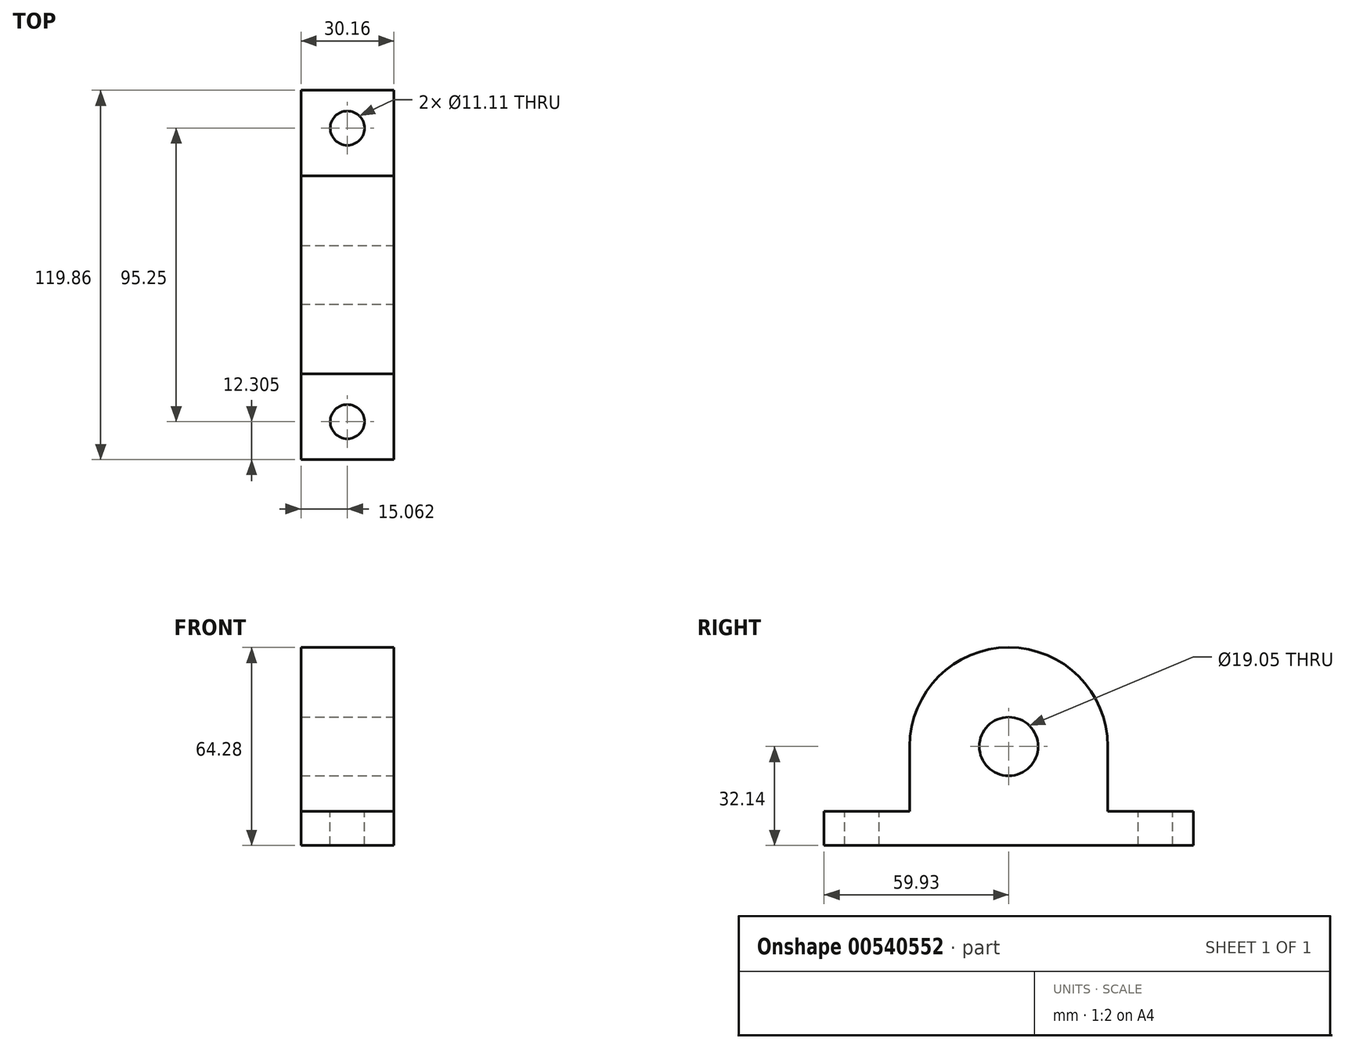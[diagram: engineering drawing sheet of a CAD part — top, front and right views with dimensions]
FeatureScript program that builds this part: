
annotation { "Feature Type Name" : "Feature", "Feature Type Description" : "" }
export const myFeature = defineFeature(function(context is Context, id is Id, definition is map)
    precondition{}
    {
        {
            var Q0;
            Q0=qCreatedBy(makeId("Right.planeOp"),FACE);
            var sketch = newSketch(context, id + "F0", { "sketchPlane" : qUnion([Q0])});
            skLineSegment(sketch, "E0.bottom", {"start": v(-59.93, 32.14) * mm, "end": v(59.93, 32.14) * mm});
            skLineSegment(sketch, "E0.top", {"start": v(-59.93, -32.14) * mm, "end": v(59.93, -32.14) * mm});
            skLineSegment(sketch, "E0.left", {"start": v(-59.93, 32.14) * mm, "end": v(-59.93, -32.14) * mm});
            skLineSegment(sketch, "E0.right", {"start": v(59.93, 32.14) * mm, "end": v(59.93, -32.14) * mm});
            skPoint(sketch, "E0.middle", {"position": v(0, 0) * mm});
            skSolve(sketch);
        }
        {
            var Q0;
            Q0 = qSketchRegion(id + "F0", true);
            extrude(context, id + "F1", {"entities" : qUnion([Q0]), "depth" : 30.16 * mm, "offsetDistance" : 25.4 * mm});
        }
        {
            var Q0;
            Q0=makeQuery(id+"F1.opExtrude","CAP_FACE",FACE,{"disambiguationData":[OSD([sQuery(id+"F0.wireOp",EDGE,"E0.bottom"),sQuery(id+"F0.wireOp",EDGE,"E0.top"),sQuery(id+"F0.wireOp",EDGE,"E0.left"),sQuery(id+"F0.wireOp",EDGE,"E0.right")])],"isStart":false});
            var sketch = newSketch(context, id + "F2", { "sketchPlane" : qUnion([Q0])});
            skCircle(sketch, "E1", {"center": v(0, 0) * mm, "radius": 9.53 * mm});
            skSolve(sketch);
        }
        {
            var Q0;
            Q0=makeQuery(id+"F2.imprint","IMPRINT",FACE,{"disambiguationData":[TD([[makeQuery(id+"F2.imprint","IMPRINT",EDGE,{"derivedFrom":sQuery(id+"F2.wireOp",EDGE,"E1")}),1.0]])]});
            extrude(context, id + "F3", {"entities" : qUnion([Q0]), "operationType" : NewBodyOperationType.REMOVE, "endBound" : BoundingType.THROUGH_ALL, "oppositeDirection" : true, "depth" : 25.4 * mm, "offsetDistance" : 25.4 * mm});
        }
        {
            var Q0;
            Q0=makeQuery(id+"F1.opExtrude","CAP_FACE",FACE,{"disambiguationData":[OSD([sQuery(id+"F0.wireOp",EDGE,"E0.bottom"),sQuery(id+"F0.wireOp",EDGE,"E0.top"),sQuery(id+"F0.wireOp",EDGE,"E0.left"),sQuery(id+"F0.wireOp",EDGE,"E0.right")])],"isStart":false});
            var sketch = newSketch(context, id + "F4", { "sketchPlane" : qUnion([Q0])});
            skSolve(sketch);
        }
        {
            var Q0;
            Q0=makeQuery(id+"F4.imprint","IMPRINT",FACE,{"disambiguationData":[TD([[makeQuery(id+"F4.imprint","IMPRINT",EDGE,{"derivedFrom":makeQuery(id+"F1.opExtrude","CAP_EDGE",EDGE,{"disambiguationData":[OSD([sQuery(id+"F0.wireOp",EDGE,"E0.bottom")])],"isStart":false})}),-1.0]])]});
            var sketch = newSketch(context, id + "F5", { "sketchPlane" : qUnion([Q0])});
            skArc(sketch, "E2", {"start": v(32.14, 0) * mm, "mid": v(0, 32.14) * mm, "end": v(-32.14, 0) * mm});
            skLineSegment(sketch, "E3", {"start": v(32.14, 0) * mm, "end": v(32.14, -21.03) * mm});
            skLineSegment(sketch, "E4", {"start": v(-32.14, 0) * mm, "end": v(-32.14, -21.03) * mm});
            skLineSegment(sketch, "E5", {"start": v(0, -32.14) * mm, "end": v(17.86, -32.14) * mm});
            skLineSegment(sketch, "E6", {"start": v(0, -32.14) * mm, "end": v(-17.86, -32.14) * mm});
            skLineSegment(sketch, "E7", {"start": v(17.86, -32.14) * mm, "end": v(17.86, -21.03) * mm});
            skLineSegment(sketch, "E8", {"start": v(-17.86, -32.14) * mm, "end": v(-17.86, -21.03) * mm});
            skLineSegment(sketch, "E9", {"start": v(17.86, -21.03) * mm, "end": v(62.7, -21.03) * mm});
            skLineSegment(sketch, "E10", {"start": v(62.7, -21.03) * mm, "end": v(62.7, -32.14) * mm});
            skLineSegment(sketch, "E11", {"start": v(62.7, -32.14) * mm, "end": v(17.86, -32.14) * mm});
            skLineSegment(sketch, "E12", {"start": v(-17.86, -21.03) * mm, "end": v(-63.4, -21.03) * mm});
            skLineSegment(sketch, "E13", {"start": v(-63.4, -21.03) * mm, "end": v(-63.4, -32.14) * mm});
            skLineSegment(sketch, "E14", {"start": v(-63.4, -32.14) * mm, "end": v(-17.86, -32.14) * mm});
            skSolve(sketch);
        }
        {
            var Q0;
            {var subQ1=sQuery(id+"F5.wireOp",EDGE,"E3");Q0=makeQuery(id+"F5.imprint","IMPRINT",FACE,{"disambiguationData":[TD([[makeQuery(id+"F5.imprint","IMPRINT",EDGE,{"derivedFrom":subQ1}),1.0]])]});}
            var sketch = newSketch(context, id + "F6", { "sketchPlane" : qUnion([Q0])});
            skSolve(sketch);
        }
        {
            var Q0;
            {var subQ1=sQuery(id+"F5.wireOp",EDGE,"E4");Q0=makeQuery(id+"F5.imprint","IMPRINT",FACE,{"disambiguationData":[TD([[makeQuery(id+"F5.imprint","IMPRINT",EDGE,{"derivedFrom":subQ1}),-1.0]])]});}
            extrude(context, id + "F7", {"entities" : qUnion([Q0]), "operationType" : NewBodyOperationType.REMOVE, "endBound" : BoundingType.THROUGH_ALL, "oppositeDirection" : true, "depth" : 25.4 * mm, "offsetDistance" : 25.4 * mm});
        }
        {
            var Q0;
            {var subQ6=sQuery(id+"F5.wireOp",EDGE,"E3");Q0=makeQuery(id+"F6.imprint","IMPRINT",FACE,{"disambiguationData":[TD([[makeQuery(id+"F6.imprint","IMPRINT",EDGE,{"derivedFrom":makeQuery(id+"F5.imprint","IMPRINT",EDGE,{"derivedFrom":subQ6})}),1.0]])]});}
            extrude(context, id + "F8", {"entities" : qUnion([Q0]), "operationType" : NewBodyOperationType.REMOVE, "endBound" : BoundingType.THROUGH_ALL, "oppositeDirection" : true, "depth" : 25.4 * mm, "offsetDistance" : 25.4 * mm});
        }
        {
            var Q0;
            Q0=qCreatedBy(makeId("Top.planeOp"),FACE);
            var sketch = newSketch(context, id + "F9", { "sketchPlane" : qUnion([Q0])});
            skCircle(sketch, "E15", {"center": v(15.06, -47.63) * mm, "radius": 5.56 * mm});
            skCircle(sketch, "E16", {"center": v(15.06, 47.63) * mm, "radius": 5.56 * mm});
            skSolve(sketch);
        }
        {
            var Q0;
            Q0 = qSketchRegion(id + "F9", true);
            extrude(context, id + "F10", {"entities" : qUnion([Q0]), "operationType" : NewBodyOperationType.REMOVE, "endBound" : BoundingType.THROUGH_ALL, "oppositeDirection" : true, "depth" : 25.4 * mm, "offsetDistance" : 25.4 * mm});
        }
    });
